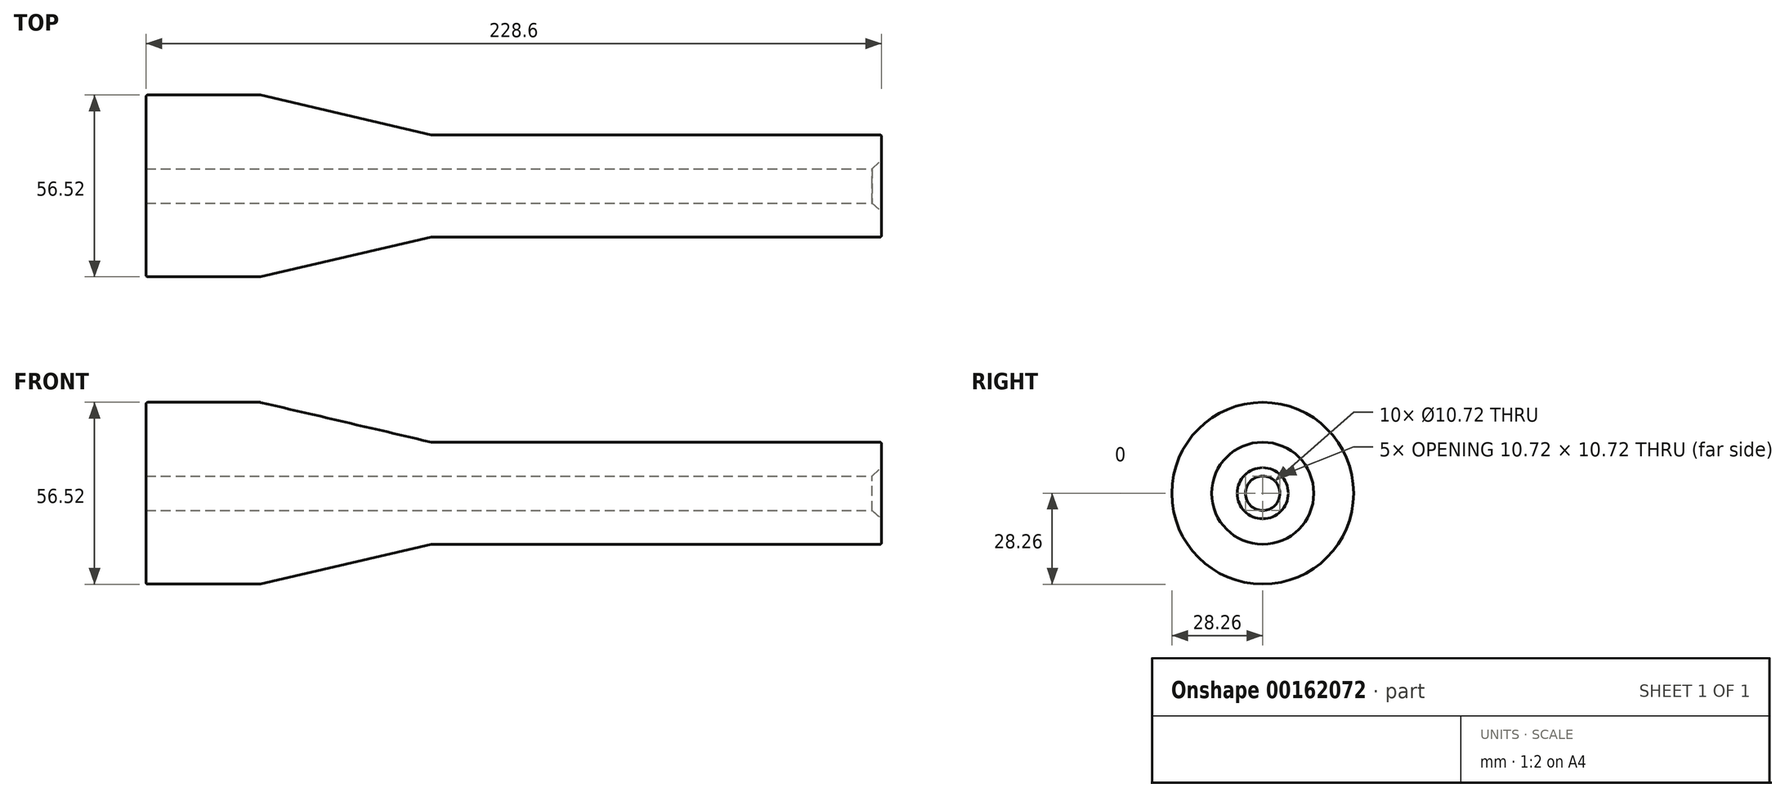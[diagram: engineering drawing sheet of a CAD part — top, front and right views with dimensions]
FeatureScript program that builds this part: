
annotation { "Feature Type Name" : "Feature", "Feature Type Description" : "" }
export const myFeature = defineFeature(function(context is Context, id is Id, definition is map)
    precondition{}
    {
        {
            var Q0;
            Q0=qCreatedBy(makeId("Front.planeOp"),FACE);
            var sketch = newSketch(context, id + "F0", { "sketchPlane" : qUnion([Q0])});
            skLineSegment(sketch, "E0", {"start": v(0, 0) * mm, "end": v(0, 28.26) * mm});
            skLineSegment(sketch, "E1", {"start": v(0, 28.26) * mm, "end": v(35.56, 28.26) * mm});
            skLineSegment(sketch, "E2", {"start": v(35.56, 28.26) * mm, "end": v(88.65, 15.87) * mm});
            skLineSegment(sketch, "E3", {"start": v(88.65, 15.87) * mm, "end": v(228.6, 15.87) * mm});
            skLineSegment(sketch, "E4", {"start": v(228.6, 15.87) * mm, "end": v(228.6, 0) * mm});
            skLineSegment(sketch, "E5", {"start": v(0, 0) * mm, "end": v(228.6, 0) * mm});
            skSolve(sketch);
        }
        {
            var Q0;
            Q0 = qSketchRegion(id + "F0", true);
            var Q1;
            Q1=sQuery(id+"F0.wireOp",EDGE,"E5");
            revolve(context, id + "F1", {"entities" : qUnion([Q0]), "axis" : qUnion([Q1]), "revolveType" : RevolveType.FULL});
        }
        {
            var Q0;
            Q0=makeQuery(id+"F1.opRevolve","SWEPT_FACE",FACE,{"disambiguationData":[OSD([sQuery(id+"F0.wireOp",EDGE,"E4")])]});
            var sketch = newSketch(context, id + "F2", { "sketchPlane" : qUnion([Q0])});
            skPoint(sketch, "E6", {"position": v(0, 0) * mm});
            skSolve(sketch);
        }
        {
            var Q0;
            Q0=sQuery(id+"F2.wireOp",VERTEX,"E6");
            var Q1;
            Q1=makeQuery(id+"F1.opRevolve","SWEPT_BODY",BODY,{"disambiguationData":[OSD([sQuery(id+"F0.wireOp",EDGE,"E0"),sQuery(id+"F0.wireOp",EDGE,"E1"),sQuery(id+"F0.wireOp",EDGE,"E2"),sQuery(id+"F0.wireOp",EDGE,"E3"),sQuery(id+"F0.wireOp",EDGE,"E4"),sQuery(id+"F0.wireOp",EDGE,"E5")])]});
            hole(context, id + "F3", {"style" : HoleStyle.C_SINK, "endStyle" : HoleEndStyle.BLIND, "holeDiameter" : 10.72 * mm, "cSinkDiameter" : 15.88 * mm, "cSinkAngle" : 82 * degree, "holeDepth" : 38.1 * mm, "locations" : qUnion([Q0]), "scope" : qUnion([Q1])});
        }
        {
            var Q0;
            Q0=makeQuery(id+"F1.opRevolve","SWEPT_FACE",FACE,{"disambiguationData":[OSD([sQuery(id+"F0.wireOp",EDGE,"E0")])]});
            var sketch = newSketch(context, id + "F4", { "sketchPlane" : qUnion([Q0])});
            skPoint(sketch, "E7", {"position": v(0, 0) * mm});
            skSolve(sketch);
        }
        {
            var Q0;
            Q0=sQuery(id+"F4.wireOp",VERTEX,"E7");
            var Q1;
            Q1=makeQuery(id+"F1.opRevolve","SWEPT_BODY",BODY,{"disambiguationData":[OSD([sQuery(id+"F0.wireOp",EDGE,"E0"),sQuery(id+"F0.wireOp",EDGE,"E1"),sQuery(id+"F0.wireOp",EDGE,"E2"),sQuery(id+"F0.wireOp",EDGE,"E3"),sQuery(id+"F0.wireOp",EDGE,"E4"),sQuery(id+"F0.wireOp",EDGE,"E5")])]});
            hole(context, id + "F5", {"style" : HoleStyle.SIMPLE, "endStyle" : HoleEndStyle.BLIND, "holeDiameter" : 10.72 * mm, "holeDepth" : 191 * mm, "locations" : qUnion([Q0]), "scope" : qUnion([Q1])});
        }
        {
            var Q0;
            Q0=makeQuery(id+"F1.opRevolve","SWEPT_EDGE",EDGE,{"disambiguationData":[OSD([sQuery(id+"F0.wireOp",EDGE,"E0"),sQuery(id+"F0.wireOp",EDGE,"E1")])]});
            var Q1;
            Q1=makeQuery(id+"F1.opRevolve","SWEPT_EDGE",EDGE,{"disambiguationData":[OSD([sQuery(id+"F0.wireOp",EDGE,"E1"),sQuery(id+"F0.wireOp",EDGE,"E2")])]});
            var Q2;
            Q2=makeQuery(id+"F1.opRevolve","SWEPT_EDGE",EDGE,{"disambiguationData":[OSD([sQuery(id+"F0.wireOp",EDGE,"E2"),sQuery(id+"F0.wireOp",EDGE,"E3")])]});
            var Q3;
            Q3=makeQuery(id+"F1.opRevolve","SWEPT_EDGE",EDGE,{"disambiguationData":[OSD([sQuery(id+"F0.wireOp",EDGE,"E3"),sQuery(id+"F0.wireOp",EDGE,"E4")])]});
            fillet(context, id + "F6", {"entities" : qUnion([Q0, Q1, Q2, Q3]), "radius" : 0.5 * mm, "tangentPropagation" : true, "allowEdgeOverflow" : false});
        }
    });
